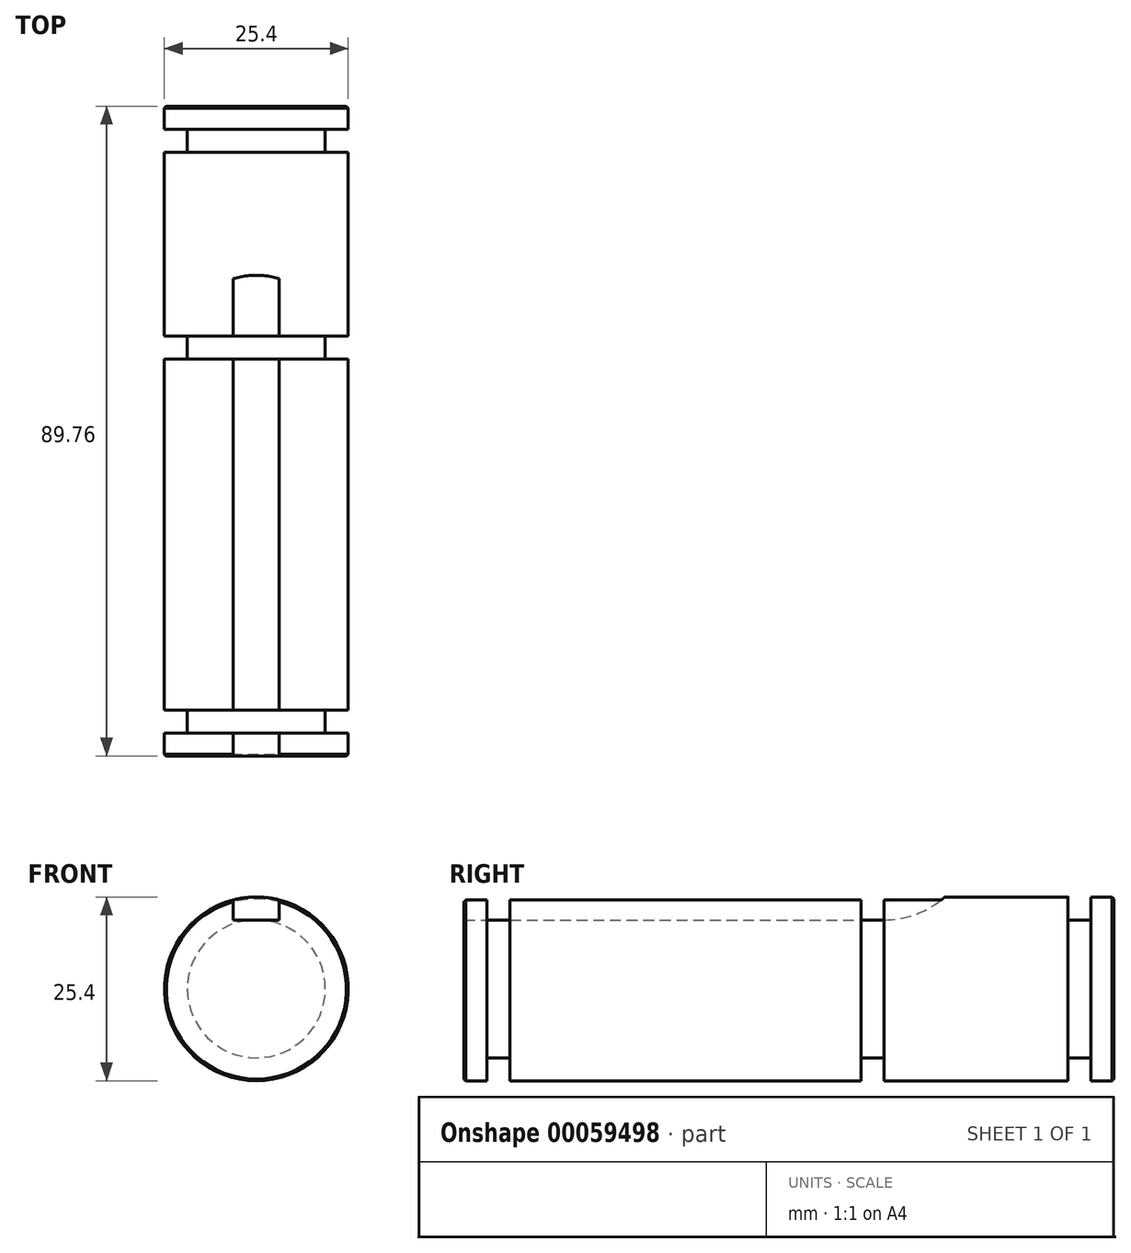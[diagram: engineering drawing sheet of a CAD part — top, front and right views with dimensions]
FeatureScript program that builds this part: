
annotation { "Feature Type Name" : "Feature", "Feature Type Description" : "" }
export const myFeature = defineFeature(function(context is Context, id is Id, definition is map)
    precondition{}
    {
        {
            var Q0;
            Q0=qCreatedBy(makeId("Front.planeOp"),FACE);
            var sketch = newSketch(context, id + "F0", { "sketchPlane" : qUnion([Q0])});
            skCircle(sketch, "E0", {"center": v(0, 0) * mm, "radius": 12.7 * mm});
            skSolve(sketch);
        }
        {
            var Q0;
            Q0=makeQuery(id+"F0.imprint","IMPRINT",FACE,{"disambiguationData":[TD([[makeQuery(id+"F0.imprint","IMPRINT",EDGE,{"derivedFrom":sQuery(id+"F0.wireOp",EDGE,"E0")}),1.0]])]});
            extrude(context, id + "F1", {"entities" : qUnion([Q0]), "oppositeDirection" : true, "depth" : 89.76 * mm});
        }
        {
            var Q0;
            Q0=qCreatedBy(makeId("Right.planeOp"),FACE);
            var sketch = newSketch(context, id + "F2", { "sketchPlane" : qUnion([Q0])});
            skLineSegment(sketch, "E1.bottom", {"start": v(0, 9.53) * mm, "end": v(58.01, 9.53) * mm});
            skLineSegment(sketch, "E1.top", {"start": v(0, 12.7) * mm, "end": v(66.41, 12.7) * mm});
            skLineSegment(sketch, "E1.left", {"start": v(0, 9.53) * mm, "end": v(0, 12.7) * mm});
            skArc(sketch, "E2.filletArc", {"start": v(58.01, 9.53) * mm, "mid": v(62.5, 10.35) * mm, "end": v(66.41, 12.7) * mm});
            skSolve(sketch);
        }
        {
            var Q0;
            Q0 = qSketchRegion(id + "F2", true);
            extrude(context, id + "F3", {"entities" : qUnion([Q0]), "operationType" : NewBodyOperationType.REMOVE, "oppositeDirection" : true, "depth" : 6.35 * mm, "symmetric" : true});
        }
        {
            var Q0;
            Q0=qCreatedBy(makeId("Right.planeOp"),FACE);
            var sketch = newSketch(context, id + "F4", { "sketchPlane" : qUnion([Q0])});
            skLineSegment(sketch, "E3.bottom", {"start": v(3.17, 9.53) * mm, "end": v(6.35, 9.53) * mm});
            skLineSegment(sketch, "E3.top", {"start": v(3.17, 12.7) * mm, "end": v(6.35, 12.7) * mm});
            skLineSegment(sketch, "E3.left", {"start": v(3.17, 9.53) * mm, "end": v(3.17, 12.7) * mm});
            skLineSegment(sketch, "E3.right", {"start": v(6.35, 9.53) * mm, "end": v(6.35, 12.7) * mm});
            skLineSegment(sketch, "E4.bottom", {"start": v(54.84, 9.53) * mm, "end": v(58.01, 9.53) * mm});
            skLineSegment(sketch, "E4.top", {"start": v(54.84, 12.7) * mm, "end": v(58.01, 12.7) * mm});
            skLineSegment(sketch, "E4.left", {"start": v(54.84, 9.53) * mm, "end": v(54.84, 12.7) * mm});
            skLineSegment(sketch, "E4.right", {"start": v(58.01, 9.53) * mm, "end": v(58.01, 12.7) * mm});
            skLineSegment(sketch, "E5.bottom", {"start": v(83.41, 9.53) * mm, "end": v(86.59, 9.53) * mm});
            skLineSegment(sketch, "E5.top", {"start": v(83.41, 12.7) * mm, "end": v(86.59, 12.7) * mm});
            skLineSegment(sketch, "E5.left", {"start": v(83.41, 9.53) * mm, "end": v(83.41, 12.7) * mm});
            skLineSegment(sketch, "E5.right", {"start": v(86.59, 9.53) * mm, "end": v(86.59, 12.7) * mm});
            skLineSegment(sketch, "E6", {"start": v(0, 0) * mm, "end": v(89.76, 0) * mm, "construction": true});
            skSolve(sketch);
        }
        {
            var Q0;
            Q0 = qSketchRegion(id + "F4", true);
            var Q1;
            Q1=sQuery(id+"F4.wireOp",EDGE,"E6");
            revolve(context, id + "F5", {"operationType" : NewBodyOperationType.REMOVE, "entities" : qUnion([Q0]), "axis" : qUnion([Q1]), "revolveType" : RevolveType.FULL, "oppositeDirection" : true});
        }
        {
            var Q0;
            Q0=makeQuery(id+"F1.opExtrude","CAP_EDGE",EDGE,{"disambiguationData":[OSD([sQuery(id+"F0.wireOp",EDGE,"E0")])],"isStart":true});
            var Q1;
            Q1=makeQuery(id+"F5.boolean.opBoolean","COPY",EDGE,{"derivedFrom":makeQuery(id+"F5.opRevolve","SWEPT_EDGE",EDGE,{"disambiguationData":[OSD([sQuery(id+"F4.wireOp",EDGE,"E3.top"),sQuery(id+"F4.wireOp",EDGE,"E3.right")])]})});
            var Q2;
            Q2=makeQuery(id+"F5.boolean.opBoolean","COPY",EDGE,{"derivedFrom":makeQuery(id+"F5.opRevolve","SWEPT_EDGE",EDGE,{"disambiguationData":[OSD([sQuery(id+"F4.wireOp",EDGE,"E4.top"),sQuery(id+"F4.wireOp",EDGE,"E4.left")])]})});
            var Q3;
            Q3=makeQuery(id+"F5.boolean.opBoolean","COPY",EDGE,{"derivedFrom":makeQuery(id+"F5.opRevolve","SWEPT_EDGE",EDGE,{"disambiguationData":[OSD([sQuery(id+"F4.wireOp",EDGE,"E4.top"),sQuery(id+"F4.wireOp",EDGE,"E4.right")])]})});
            var Q4;
            Q4=makeQuery(id+"F5.boolean.opBoolean","COPY",EDGE,{"derivedFrom":makeQuery(id+"F5.opRevolve","SWEPT_EDGE",EDGE,{"disambiguationData":[OSD([sQuery(id+"F4.wireOp",EDGE,"E5.top"),sQuery(id+"F4.wireOp",EDGE,"E5.left")])]})});
            var Q5;
            Q5=makeQuery(id+"F5.boolean.opBoolean","COPY",EDGE,{"derivedFrom":makeQuery(id+"F5.opRevolve","SWEPT_EDGE",EDGE,{"disambiguationData":[OSD([sQuery(id+"F4.wireOp",EDGE,"E5.top"),sQuery(id+"F4.wireOp",EDGE,"E5.right")])]})});
            var Q6;
            Q6=makeQuery(id+"F1.opExtrude","CAP_EDGE",EDGE,{"disambiguationData":[OSD([sQuery(id+"F0.wireOp",EDGE,"E0")])],"isStart":false});
            chamfer(context, id + "F6", {"entities" : qUnion([Q0, Q1, Q2, Q3, Q4, Q5, Q6]), "width" : 0.25 * mm, "tangentPropagation" : true});
        }
    });
